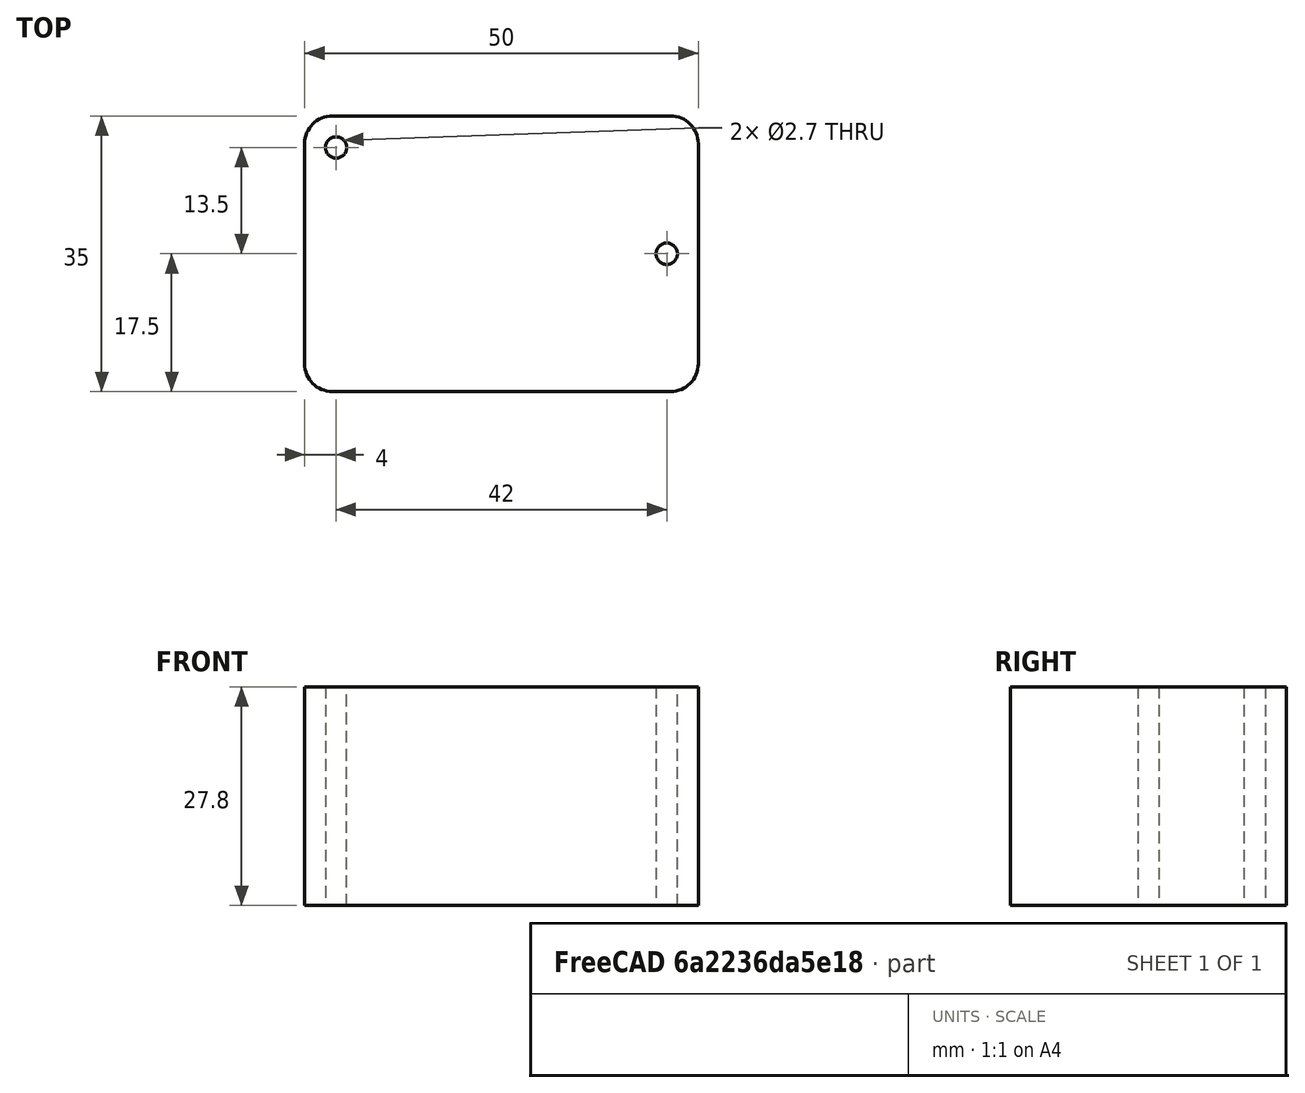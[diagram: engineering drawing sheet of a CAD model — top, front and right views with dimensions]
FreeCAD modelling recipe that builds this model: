
FCSTD DOCUMENT  (FreeCAD 0.18.4R)
Label: MJ_CES-503528-28PM-67
License: All rights reserved
LicenseURL: http://en.wikipedia.org/wiki/All_rights_reserved
objects: Sketcher::SketchObject×1, PartDesign::Pad×1, PartDesign::Body×1
note: 4 computed .brp shape members not serialized (recipe doc carries the construction recipe); baked Part::Feature solids carry a one-line shape summary decoded from their .brp

FEATURE [Sketcher::SketchObject] Sketch
  MapMode = 5
  Support = -> [XY_Plane]
  sketch-geometry (10):
    g0: LineSegment StartX=-21.5 StartY=17.5 StartZ=0 EndX=21.5 EndY=17.5 EndZ=0
    g1: LineSegment StartX=25 StartY=14 StartZ=0 EndX=25 EndY=-14 EndZ=0
    g2: LineSegment StartX=21.5 StartY=-17.5 StartZ=0 EndX=-21.5 EndY=-17.5 EndZ=0
    g3: LineSegment StartX=-25 StartY=-14 StartZ=0 EndX=-25 EndY=14 EndZ=0
    g4: ArcOfCircle CenterX=-21.5 CenterY=14 CenterZ=0 NormalX=0 NormalY=0 NormalZ=1 AngleXU=0 Radius=3.5 StartAngle=1.5708 EndAngle=3.14159
    g5: ArcOfCircle CenterX=21.5 CenterY=14 CenterZ=0 NormalX=0 NormalY=0 NormalZ=1 AngleXU=0 Radius=3.5 StartAngle=1.6e-15 EndAngle=1.5708
    g6: ArcOfCircle CenterX=21.5 CenterY=-14 CenterZ=0 NormalX=0 NormalY=0 NormalZ=1 AngleXU=0 Radius=3.5 StartAngle=4.71239 EndAngle=6.28319
    g7: ArcOfCircle CenterX=-21.5 CenterY=-14 CenterZ=0 NormalX=0 NormalY=0 NormalZ=1 AngleXU=0 Radius=3.5 StartAngle=3.14159 EndAngle=4.71239
    g8: Circle CenterX=21 CenterY=0 CenterZ=0 NormalX=0 NormalY=0 NormalZ=1 AngleXU=0 Radius=1.35
    g9: Circle CenterX=-21 CenterY=13.5 CenterZ=0 NormalX=0 NormalY=0 NormalZ=1 AngleXU=0 Radius=1.35
  constraints (24):
    c: Horizontal(g0)
    c: Horizontal(g2)
    c: Vertical(g1)
    c: Vertical(g3)
    c: Tangent(g3,g4) = 1.5708
    c: Tangent(g0,g4) = 1.5708
    c: Tangent(g0,g5) = 1.5708
    c: Tangent(g1,g5) = 1.5708
    c: Tangent(g1,g6) = 1.5708
    c: Tangent(g2,g6) = 1.5708
    c: Tangent(g2,g7) = 1.5708
    c: Tangent(g3,g7) = 1.5708
    c: Equal(g5,g6)
    c: Radius(g5) = 3.5
    c: DistanceX(g3,g1) = 50
    c: DistanceY(g2,g0) = 35
    c: Symmetric(g0,g2,g-1)
    c: Symmetric(g3,g1,g-2)
    c: PointOnObject(g8,g-1)
    c: Equal(g9,g8)
    c: Diameter(g8) = 2.7
    c: DistanceY(g8,g9) = 13.5
    c: DistanceX(g9,g8) = 42
    c: DistanceX(g9,g-1) = 21
FEATURE [PartDesign::Pad] Pad
  Length = 27.8
  Length2 = 100
  Profile = -> Sketch
  Type = 0
FEATURE [PartDesign::Body] Body
  Group = -> [Sketch,Pad]
  Origin = -> Origin
  Tip = -> Pad
